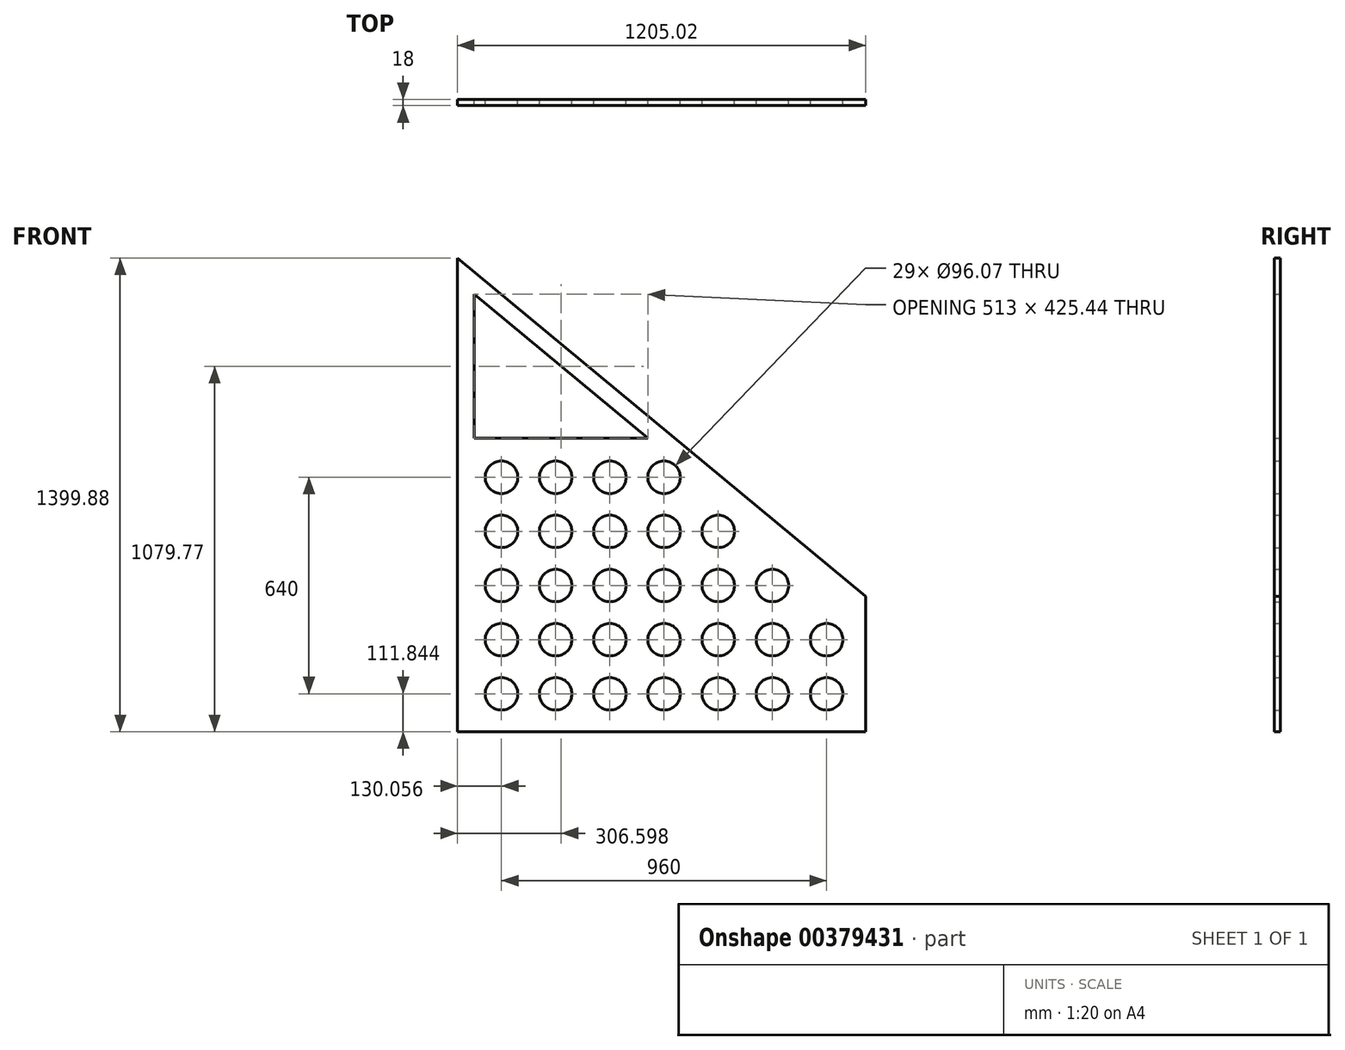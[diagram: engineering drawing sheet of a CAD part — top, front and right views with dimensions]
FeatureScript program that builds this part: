
annotation { "Feature Type Name" : "Feature", "Feature Type Description" : "" }
export const myFeature = defineFeature(function(context is Context, id is Id, definition is map)
    precondition{}
    {
        {
            var Q0;
            Q0=qCreatedBy(makeId("Front.planeOp"),FACE);
            var sketch = newSketch(context, id + "F0", { "sketchPlane" : qUnion([Q0])});
            skLineSegment(sketch, "E0", {"start": v(52.93, -39.5) * mm, "end": v(-1152.1, -39.5) * mm});
            skLineSegment(sketch, "E1", {"start": v(-1152.1, -39.5) * mm, "end": v(-1152.1, 1360.38) * mm});
            skLineSegment(sketch, "E2", {"start": v(52.93, -39.5) * mm, "end": v(52.93, 361.02) * mm});
            skLineSegment(sketch, "E3", {"start": v(52.93, 361.02) * mm, "end": v(-1152.1, 1360.38) * mm});
            skCircle(sketch, "E4", {"center": v(-62.03, 72.34) * mm, "radius": 48.04 * mm});
            skCircle(sketch, "E5.0.1.0", {"center": v(-62.03, 232.34) * mm, "radius": 48.04 * mm});
            skCircle(sketch, "E5.1.0.0", {"center": v(-222.03, 72.34) * mm, "radius": 48.04 * mm});
            skCircle(sketch, "E5.1.1.0", {"center": v(-222.03, 232.34) * mm, "radius": 48.04 * mm});
            skCircle(sketch, "E5.1.2.0", {"center": v(-222.03, 392.34) * mm, "radius": 48.04 * mm});
            skCircle(sketch, "E5.2.0.0", {"center": v(-382.03, 72.34) * mm, "radius": 48.04 * mm});
            skCircle(sketch, "E5.2.1.0", {"center": v(-382.03, 232.34) * mm, "radius": 48.04 * mm});
            skCircle(sketch, "E5.2.2.0", {"center": v(-382.03, 392.34) * mm, "radius": 48.04 * mm});
            skCircle(sketch, "E5.2.3.0", {"center": v(-382.03, 552.34) * mm, "radius": 48.04 * mm});
            skCircle(sketch, "E5.3.0.0", {"center": v(-542.03, 72.34) * mm, "radius": 48.04 * mm});
            skCircle(sketch, "E5.3.1.0", {"center": v(-542.03, 232.34) * mm, "radius": 48.04 * mm});
            skCircle(sketch, "E5.3.2.0", {"center": v(-542.03, 392.34) * mm, "radius": 48.04 * mm});
            skCircle(sketch, "E5.3.3.0", {"center": v(-542.03, 552.34) * mm, "radius": 48.04 * mm});
            skCircle(sketch, "E5.3.4.0", {"center": v(-542.03, 712.34) * mm, "radius": 48.04 * mm});
            skCircle(sketch, "E5.4.0.0", {"center": v(-702.03, 72.34) * mm, "radius": 48.04 * mm});
            skCircle(sketch, "E5.4.1.0", {"center": v(-702.03, 232.34) * mm, "radius": 48.04 * mm});
            skCircle(sketch, "E5.4.2.0", {"center": v(-702.03, 392.34) * mm, "radius": 48.04 * mm});
            skCircle(sketch, "E5.4.3.0", {"center": v(-702.03, 552.34) * mm, "radius": 48.04 * mm});
            skCircle(sketch, "E5.4.4.0", {"center": v(-702.03, 712.34) * mm, "radius": 48.04 * mm});
            skCircle(sketch, "E5.5.0.0", {"center": v(-862.03, 72.34) * mm, "radius": 48.04 * mm});
            skCircle(sketch, "E5.5.1.0", {"center": v(-862.03, 232.34) * mm, "radius": 48.04 * mm});
            skCircle(sketch, "E5.5.2.0", {"center": v(-862.03, 392.34) * mm, "radius": 48.04 * mm});
            skCircle(sketch, "E5.5.3.0", {"center": v(-862.03, 552.34) * mm, "radius": 48.04 * mm});
            skCircle(sketch, "E5.5.4.0", {"center": v(-862.03, 712.34) * mm, "radius": 48.04 * mm});
            skCircle(sketch, "E5.6.0.0", {"center": v(-1022.03, 72.34) * mm, "radius": 48.04 * mm});
            skCircle(sketch, "E5.6.1.0", {"center": v(-1022.03, 232.34) * mm, "radius": 48.04 * mm});
            skCircle(sketch, "E5.6.2.0", {"center": v(-1022.03, 392.34) * mm, "radius": 48.04 * mm});
            skCircle(sketch, "E5.6.3.0", {"center": v(-1022.03, 552.34) * mm, "radius": 48.04 * mm});
            skCircle(sketch, "E5.6.4.0", {"center": v(-1022.03, 712.34) * mm, "radius": 48.04 * mm});
            skLineSegment(sketch, "E5.direction1", {"start": v(-62.03, 72.34) * mm, "end": v(-222.03, 72.34) * mm, "construction": true});
            skLineSegment(sketch, "E5.direction2", {"start": v(-62.03, 72.34) * mm, "end": v(-62.03, 232.34) * mm, "construction": true});
            skLineSegment(sketch, "E6.trimOffspring", {"start": v(-1101.99, 827.55) * mm, "end": v(-1101.99, 1252.99) * mm});
            skLineSegment(sketch, "E7", {"start": v(-1101.99, 827.55) * mm, "end": v(-589, 827.55) * mm});
            skLineSegment(sketch, "E8", {"start": v(-1101.99, 1252.99) * mm, "end": v(-589, 827.55) * mm});
            skSolve(sketch);
        }
        {
            var Q0;
            Q0 = qSketchRegion(id + "F0", true);
            extrude(context, id + "F1", {"entities" : qUnion([Q0]), "depth" : 18 * mm});
        }
    });
